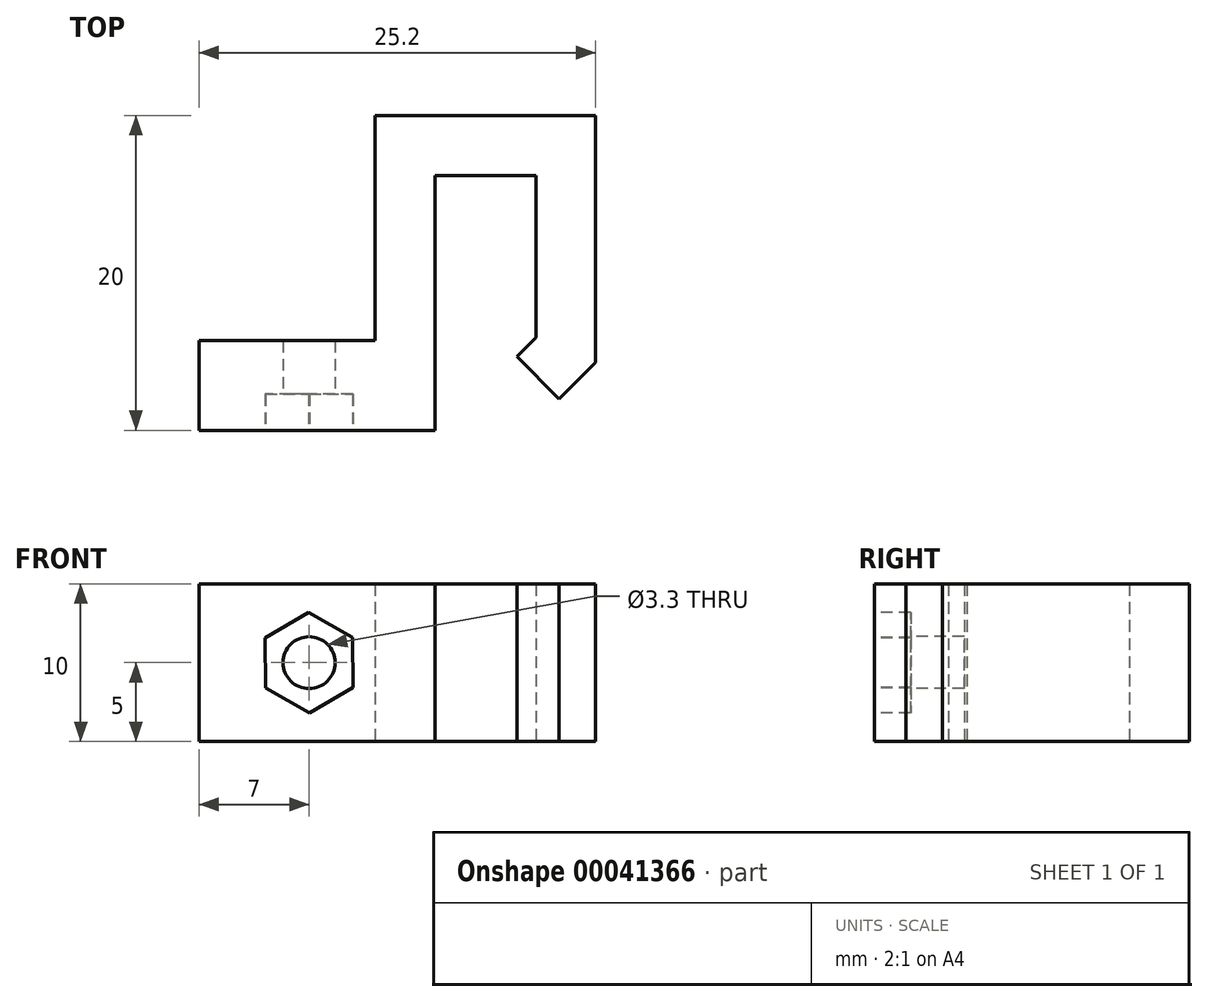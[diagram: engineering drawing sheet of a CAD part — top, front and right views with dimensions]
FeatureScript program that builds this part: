
annotation { "Feature Type Name" : "Feature", "Feature Type Description" : "" }
export const myFeature = defineFeature(function(context is Context, id is Id, definition is map)
    precondition{}
    {
        {
            var Q0;
            Q0=qCreatedBy(makeId("Top.planeOp"),FACE);
            var sketch = newSketch(context, id + "F0", { "sketchPlane" : qUnion([Q0])});
            skLineSegment(sketch, "E0", {"start": v(0, 0) * mm, "end": v(15, 0) * mm});
            skLineSegment(sketch, "E1", {"start": v(15, 0) * mm, "end": v(15, 16.2) * mm});
            skLineSegment(sketch, "E2", {"start": v(15, 16.2) * mm, "end": v(21.4, 16.2) * mm});
            skLineSegment(sketch, "E3", {"start": v(21.4, 16.2) * mm, "end": v(21.4, 5.89) * mm});
            skLineSegment(sketch, "E4", {"start": v(21.4, 5.89) * mm, "end": v(20.2, 4.69) * mm});
            skLineSegment(sketch, "E5", {"start": v(20.2, 4.69) * mm, "end": v(22.89, 2) * mm});
            skLineSegment(sketch, "E6", {"start": v(22.89, 2) * mm, "end": v(25.2, 4.31) * mm});
            skLineSegment(sketch, "E7", {"start": v(25.2, 4.31) * mm, "end": v(25.2, 20) * mm});
            skLineSegment(sketch, "E8", {"start": v(25.2, 20) * mm, "end": v(11.2, 20) * mm});
            skLineSegment(sketch, "E9", {"start": v(11.2, 20) * mm, "end": v(11.2, 5.7) * mm});
            skLineSegment(sketch, "E10", {"start": v(11.2, 5.7) * mm, "end": v(0, 5.7) * mm});
            skLineSegment(sketch, "E11", {"start": v(0, 5.7) * mm, "end": v(0, 0) * mm});
            skSolve(sketch);
        }
        {
            var Q0;
            Q0=makeQuery(id+"F0.imprint","IMPRINT",FACE,{"disambiguationData":[TD([[makeQuery(id+"F0.imprint","IMPRINT",EDGE,{"derivedFrom":sQuery(id+"F0.wireOp",EDGE,"E0")}),1.0]])]});
            extrude(context, id + "F1", {"entities" : qUnion([Q0]), "depth" : 10 * mm});
        }
        {
            var Q0;
            Q0=makeQuery(id+"F1.opExtrude","SWEPT_FACE",FACE,{"disambiguationData":[OSD([sQuery(id+"F0.wireOp",EDGE,"E0")])]});
            var sketch = newSketch(context, id + "F2", { "sketchPlane" : qUnion([Q0])});
            skLineSegment(sketch, "E12", {"start": v(0, 5) * mm, "end": v(15, 5) * mm, "construction": true});
            skCircle(sketch, "E13", {"center": v(7, 5) * mm, "radius": 1.65 * mm});
            skCircle(sketch, "E14.cCircle", {"center": v(7, 5) * mm, "radius": 3.2 * mm, "construction": true});
            skLineSegment(sketch, "E14.0", {"start": v(4.22, 6.58) * mm, "end": v(6.98, 8.2) * mm});
            skLineSegment(sketch, "E14.1", {"start": v(6.98, 8.2) * mm, "end": v(9.76, 6.62) * mm});
            skLineSegment(sketch, "E14.2", {"start": v(9.76, 6.62) * mm, "end": v(9.78, 3.42) * mm});
            skLineSegment(sketch, "E14.3", {"start": v(9.78, 3.42) * mm, "end": v(7.02, 1.8) * mm});
            skLineSegment(sketch, "E14.4", {"start": v(7.02, 1.8) * mm, "end": v(4.24, 3.38) * mm});
            skLineSegment(sketch, "E14.5", {"start": v(4.24, 3.38) * mm, "end": v(4.22, 6.58) * mm});
            skSolve(sketch);
        }
        {
            assignVariable(context, id + "F3", {"name" : "PolygonHeigth", "anyValue" : 2.3});
        }
        {
            var Q0;
            Q0=makeQuery(id+"F2.imprint","IMPRINT",FACE,{"disambiguationData":[TD([[makeQuery(id+"F2.imprint","IMPRINT",EDGE,{"derivedFrom":sQuery(id+"F2.wireOp",EDGE,"E13")}),1.0]])]});
            extrude(context, id + "F4", {"entities" : qUnion([Q0]), "operationType" : NewBodyOperationType.REMOVE, "endBound" : BoundingType.THROUGH_ALL, "oppositeDirection" : true, "depth" : 25 * mm});
        }
        {
            var Q0;
            Q0=makeQuery(id+"F2.imprint","IMPRINT",FACE,{"disambiguationData":[TD([[makeQuery(id+"F2.imprint","IMPRINT",EDGE,{"derivedFrom":sQuery(id+"F2.wireOp",EDGE,"E13")}),-1.0]])]});
            extrude(context, id + "F5", {"entities" : qUnion([Q0]), "operationType" : NewBodyOperationType.REMOVE, "oppositeDirection" : true, "depth" : (getVariable(context, 'PolygonHeigth')) * mm});
        }
    });
